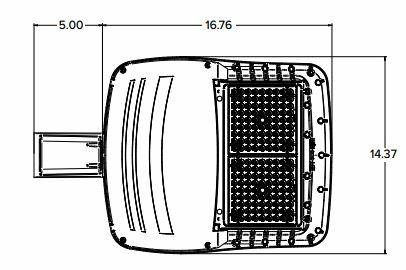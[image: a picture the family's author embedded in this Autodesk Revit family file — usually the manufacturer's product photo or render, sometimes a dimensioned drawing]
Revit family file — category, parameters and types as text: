
# Revit family: VP-3-ASQU
name_source: partatom
category: Lighting Fixtures
units: mm (PartAtom-declared; Revit-internal decimal feet)

## family parameters
Cut with Voids When Loaded = No
Host = Face
Light Source = No
OmniClass Number = 23.80.70.11.14.17
OmniClass Title = Direct/Indirect
Part Type = Normal
Room Calculation Point = No
Round Connector Dimension = Use Diameter
Shared = Yes

## types (1)
- VP-3-ASQU
    Apparent Load = 423 VA
    Assembly Code = D5020200
    Brand = Beacon
    CRI = 70
    Certification = UL
    Cool Grey = Cool Grey
    Default Elevation = 48 "
    Description = The Viper is an extremely versatile area/site luminaire which blends design, performance, and technology for a variety of applications.
    Features = Featuring two different optical technologies, Micro Strike and Strike Optics, which provide the best distribution patterns for retrofit or new construction
Vibration rated for high vibration applications including bridges and overpasses
Control options including photo control, occupancy sensing, NX Lighting Controls, wiSCAPE and 7-Pin with networked controls
Mounting options include: Arm, Universal Arm, Adjustable Arm, Mast Arm, Decorative Arm, Knuckle, Trunnion, Wall
Distribution options include: Auto Front Row, Type 2, Type 3, Type 4 Forward, Type 4 Wide, Type 5 Narrow, Type 5 Medium, Type 5 Wide, Type 5 Rectangular, Corner Optic, and Tennis Court
    Finish = Arctic White
    Glass = Glass
    Grey = Grey
    Lamp = LED
    Light Output = 30846 cd/m²
    Load Classification = Lighting
    Manufacturer = Current Lighting
    Matt Black = Matt Black
    Matt Grey = MATT GREY
    Matt White = Matt White
    Model = VP-3-ASQU
    Name = Viper Area Size 3
    Power Factor = 0.9
    Product Documentation Link = https://cdn.currentlighting.com
    Product Page URL = https://www.currentlighting.com
    Type Comments = Lighting Fixture
    URL = https://www.currentlighting.com
    Voltage = 120 V
    Warranty = Five year warranty
    Wattage Comments = 423.2W

## geometry (parser evidence)
native form markers: Blend x4, Sweep x5
no freeform markers — native parametric forms only
